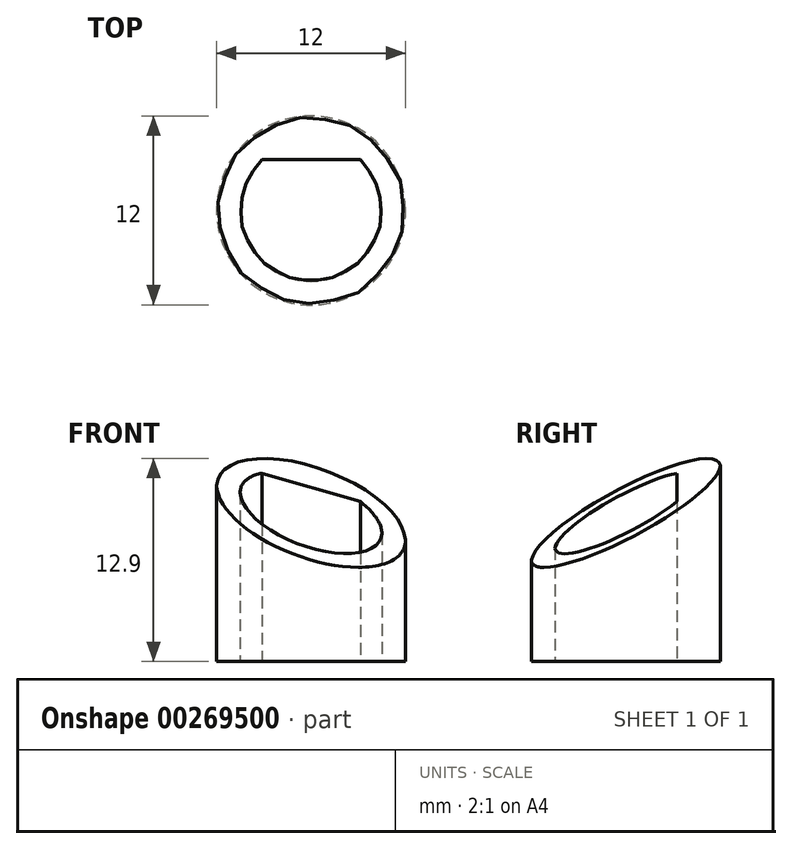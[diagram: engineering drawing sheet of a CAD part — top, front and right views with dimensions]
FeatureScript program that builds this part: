
annotation { "Feature Type Name" : "Feature", "Feature Type Description" : "" }
export const myFeature = defineFeature(function(context is Context, id is Id, definition is map)
    precondition{}
    {
        {
            var Q0;
            Q0=qCreatedBy(makeId("Top.planeOp"),FACE);
            var sketch = newSketch(context, id + "F0", { "sketchPlane" : qUnion([Q0])});
            skCircle(sketch, "E0", {"center": v(0, 0) * mm, "radius": 6 * mm});
            skCircle(sketch, "E1", {"center": v(0, 0) * mm, "radius": 4.5 * mm});
            skLineSegment(sketch, "E2", {"start": v(0, 0) * mm, "end": v(0, 12.02) * mm, "construction": true});
            skLineSegment(sketch, "E3", {"start": v(-3.13, 3.24) * mm, "end": v(3.13, 3.24) * mm});
            skSolve(sketch);
        }
        {
            var Q0;
            Q0=makeQuery(id+"F0.imprint","IMPRINT",FACE,{"disambiguationData":[TD([[makeQuery(id+"F0.imprint","IMPRINT",EDGE,{"derivedFrom":sQuery(id+"F0.wireOp",EDGE,"E0")}),1.0]])]});
            var Q1;
            {var subQ0=sQuery(id+"F0.wireOp",EDGE,"E3");Q1=makeQuery(id+"F0.imprint","IMPRINT",FACE,{"disambiguationData":[TD([[makeQuery(id+"F0.imprint","IMPRINT",EDGE,{"derivedFrom":subQ0}),1.0]])]});}
            extrude(context, id + "F1", {"entities" : qUnion([Q0, Q1]), "depth" : 15 * mm});
        }
        {
            var Q0;
            Q0=makeQuery(id+"F1.opExtrude","CAP_FACE",FACE,{"disambiguationData":[OSD([sQuery(id+"F0.wireOp",EDGE,"E0"),sQuery(id+"F0.wireOp",EDGE,"E1"),sQuery(id+"F0.wireOp",EDGE,"E3")])],"isStart":false});
            var sketch = newSketch(context, id + "F2", { "sketchPlane" : qUnion([Q0])});
            skLineSegment(sketch, "E4", {"start": v(0, 0) * mm, "end": v(0, 11.5) * mm, "construction": true});
            skPoint(sketch, "E4.endSnap0", {"position": v(0, 3.24) * mm});
            skLineSegment(sketch, "E5", {"start": v(0, 0) * mm, "end": v(-7.14, 12.36) * mm, "construction": true});
            skLineSegment(sketch, "E6", {"start": v(-3, 5.2) * mm, "end": v(-7.66, 2.5) * mm, "construction": true});
            skLineSegment(sketch, "E7", {"start": v(-3, 5.2) * mm, "end": v(-6.71, 3.05) * mm});
            skLineSegment(sketch, "E8", {"start": v(-3, 5.2) * mm, "end": v(-4.82, 8.34) * mm});
            skSolve(sketch);
        }
        {
            var Q0;
            Q0=sQuery(id+"F2.wireOp",EDGE,"E7");
            extrude(context, id + "F3", {"bodyType" : ExtendedToolBodyType.SURFACE, "surfaceEntities" : qUnion([Q0]), "oppositeDirection" : true, "depth" : 15 * mm});
        }
        {
            var Q0;
            Q0=sQuery(id+"F2.wireOp",EDGE,"E8");
            extrude(context, id + "F4", {"bodyType" : ExtendedToolBodyType.SURFACE, "surfaceEntities" : qUnion([Q0]), "oppositeDirection" : true, "depth" : 15 * mm});
        }
        {
            var Q0;
            Q0=makeQuery(id+"F4.opExtrude","SWEPT_FACE",FACE,{"disambiguationData":[OSD([sQuery(id+"F2.wireOp",EDGE,"E8")])]});
            var sketch = newSketch(context, id + "F5", { "sketchPlane" : qUnion([Q0])});
            skLineSegment(sketch, "E9", {"start": v(-9.63, 15) * mm, "end": v(8.16, 4.73) * mm, "construction": true});
            skLineSegment(sketch, "E10", {"start": v(-9.63, 15) * mm, "end": v(6.8, 15) * mm});
            skLineSegment(sketch, "E11", {"start": v(6.8, 15) * mm, "end": v(6.8, 5.5) * mm});
            skLineSegment(sketch, "E12", {"start": v(6.8, 5.5) * mm, "end": v(-9.63, 15) * mm});
            skSolve(sketch);
        }
        {
            var Q0;
            {var subQ3=sQuery(id+"F5.wireOp",EDGE,"E11");Q0=makeQuery(id+"F5.imprint","IMPRINT",FACE,{"disambiguationData":[TD([[makeQuery(id+"F5.imprint","IMPRINT",EDGE,{"derivedFrom":subQ3}),-1.0]])]});}
            extrude(context, id + "F6", {"entities" : qUnion([Q0]), "operationType" : NewBodyOperationType.REMOVE, "depth" : 25 * mm, "symmetric" : true});
        }
    });
